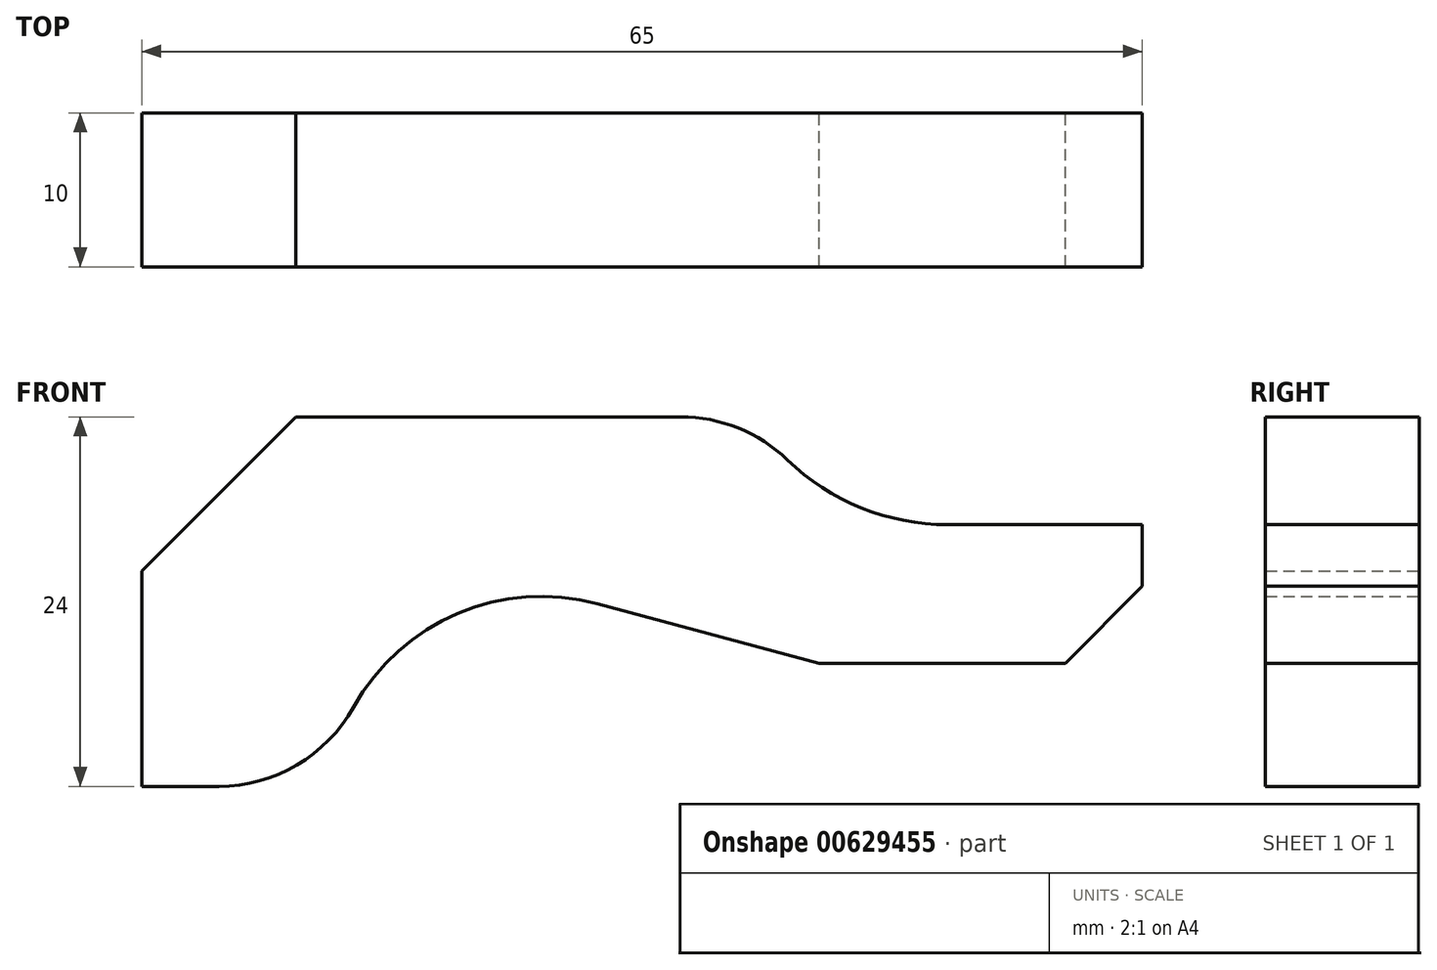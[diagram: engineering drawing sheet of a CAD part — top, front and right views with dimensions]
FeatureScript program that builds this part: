
annotation { "Feature Type Name" : "Feature", "Feature Type Description" : "" }
export const myFeature = defineFeature(function(context is Context, id is Id, definition is map)
    precondition{}
    {
        {
            var Q0;
            Q0=qCreatedBy(makeId("Front.planeOp"),FACE);
            var sketch = newSketch(context, id + "F0", { "sketchPlane" : qUnion([Q0])});
            skLineSegment(sketch, "E0", {"start": v(0, 0) * mm, "end": v(0, 14) * mm});
            skLineSegment(sketch, "E1", {"start": v(0, 14) * mm, "end": v(10, 24) * mm});
            skLineSegment(sketch, "E2", {"start": v(10, 24) * mm, "end": v(35, 24) * mm});
            skArc(sketch, "E3", {"start": v(35, 24) * mm, "mid": v(38.74, 23.27) * mm, "end": v(41.94, 21.2) * mm});
            skArc(sketch, "E4", {"start": v(41.94, 21.2) * mm, "mid": v(46.74, 18.09) * mm, "end": v(52.35, 17) * mm});
            skLineSegment(sketch, "E5", {"start": v(52.35, 17) * mm, "end": v(65, 17) * mm});
            skLineSegment(sketch, "E6", {"start": v(65, 17) * mm, "end": v(65, 13) * mm});
            skLineSegment(sketch, "E7", {"start": v(65, 13) * mm, "end": v(60, 8) * mm});
            skLineSegment(sketch, "E8", {"start": v(60, 8) * mm, "end": v(44, 8) * mm});
            skLineSegment(sketch, "E9", {"start": v(44, 8) * mm, "end": v(29.6, 11.86) * mm});
            skArc(sketch, "E10", {"start": v(29.6, 11.86) * mm, "mid": v(20.51, 11.23) * mm, "end": v(13.74, 5.14) * mm});
            skArc(sketch, "E11", {"start": v(13.74, 5.14) * mm, "mid": v(10.07, 1.38) * mm, "end": v(5, 0) * mm});
            skLineSegment(sketch, "E12", {"start": v(0, 0) * mm, "end": v(5, 0) * mm});
            skSolve(sketch);
        }
        {
            var Q0;
            Q0=makeQuery(id+"F0.imprint","IMPRINT",FACE,{"disambiguationData":[TD([[makeQuery(id+"F0.imprint","IMPRINT",EDGE,{"derivedFrom":sQuery(id+"F0.wireOp",EDGE,"E0")}),-1.0]])]});
            extrude(context, id + "F1", {"entities" : qUnion([Q0]), "depth" : 10 * mm, "offsetDistance" : 25 * mm, "symmetric" : true});
        }
    });
